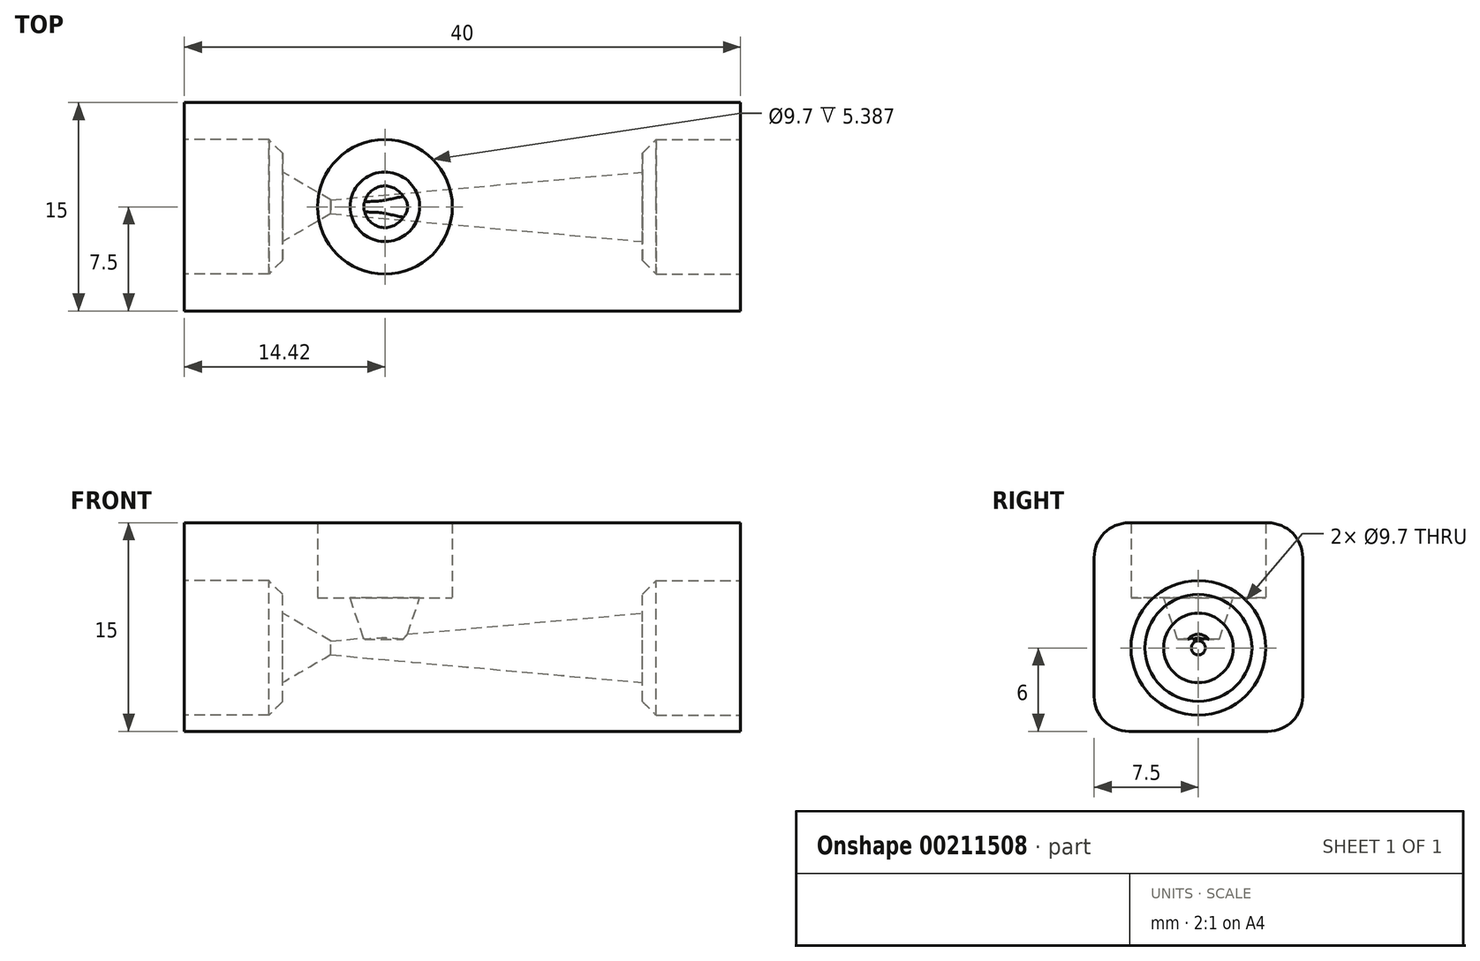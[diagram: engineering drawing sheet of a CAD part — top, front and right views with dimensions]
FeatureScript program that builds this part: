
annotation { "Feature Type Name" : "Feature", "Feature Type Description" : "" }
export const myFeature = defineFeature(function(context is Context, id is Id, definition is map)
    precondition{}
    {
        {
            var Q0;
            Q0=qCreatedBy(makeId("Right.planeOp"),FACE);
            var sketch = newSketch(context, id + "F0", { "sketchPlane" : qUnion([Q0])});
            skLineSegment(sketch, "E0.bottom", {"start": v(5, 7.5) * mm, "end": v(-5, 7.5) * mm});
            skLineSegment(sketch, "E0.top", {"start": v(5, -7.5) * mm, "end": v(-5, -7.5) * mm});
            skLineSegment(sketch, "E0.left", {"start": v(7.5, 5) * mm, "end": v(7.5, -5) * mm});
            skLineSegment(sketch, "E0.right", {"start": v(-7.5, 5) * mm, "end": v(-7.5, -5) * mm});
            skPoint(sketch, "E0.middle", {"position": v(0, 0) * mm});
            skPoint(sketch, "E1.visualSharp", {"position": v(-7.5, 7.5) * mm});
            skArc(sketch, "E1.filletArc", {"start": v(-5, 7.5) * mm, "mid": v(-6.77, 6.77) * mm, "end": v(-7.5, 5) * mm});
            skPoint(sketch, "E2.visualSharp", {"position": v(7.5, 7.5) * mm});
            skArc(sketch, "E2.filletArc", {"start": v(7.5, 5) * mm, "mid": v(6.77, 6.77) * mm, "end": v(5, 7.5) * mm});
            skPoint(sketch, "E3.visualSharp", {"position": v(7.5, -7.5) * mm});
            skArc(sketch, "E3.filletArc", {"start": v(5, -7.5) * mm, "mid": v(6.77, -6.77) * mm, "end": v(7.5, -5) * mm});
            skPoint(sketch, "E4.visualSharp", {"position": v(-7.5, -7.5) * mm});
            skArc(sketch, "E4.filletArc", {"start": v(-7.5, -5) * mm, "mid": v(-6.77, -6.77) * mm, "end": v(-5, -7.5) * mm});
            skSolve(sketch);
        }
        {
            var Q0;
            Q0=makeQuery(id+"F0.imprint","IMPRINT",FACE,{"disambiguationData":[TD([[makeQuery(id+"F0.imprint","IMPRINT",EDGE,{"derivedFrom":sQuery(id+"F0.wireOp",EDGE,"E0.left")}),-1.0]])]});
            extrude(context, id + "F1", {"entities" : qUnion([Q0]), "depth" : 40 * mm});
        }
        {
            var Q0;
            Q0=makeQuery(id+"F1.opExtrude","CAP_FACE",FACE,{"disambiguationData":[OSD([sQuery(id+"F0.wireOp",EDGE,"E0.left"),sQuery(id+"F0.wireOp",EDGE,"E0.right"),sQuery(id+"F0.wireOp",EDGE,"E1.filletArc"),sQuery(id+"F0.wireOp",EDGE,"E2.filletArc"),sQuery(id+"F0.wireOp",EDGE,"E3.filletArc"),sQuery(id+"F0.wireOp",EDGE,"E4.filletArc")])],"isStart":false});
            var sketch = newSketch(context, id + "F2", { "sketchPlane" : qUnion([Q0])});
            skCircle(sketch, "E5", {"center": v(0, -1.5) * mm, "radius": 4.85 * mm});
            skSolve(sketch);
        }
        {
            var Q0;
            Q0=makeQuery(id+"F2.imprint","IMPRINT",FACE,{"disambiguationData":[TD([[makeQuery(id+"F2.imprint","IMPRINT",EDGE,{"derivedFrom":sQuery(id+"F2.wireOp",EDGE,"pYlIlDuR-fTkt-dUTK-9zJj-bOiV4e9yzW8T")}),1.0]])]});
            var Q1;
            Q1=makeQuery(id+"F2.imprint","IMPRINT",FACE,{"disambiguationData":[TD([[makeQuery(id+"F2.imprint","IMPRINT",EDGE,{"derivedFrom":sQuery(id+"F2.wireOp",EDGE,"E5")}),1.0]])]});
            extrude(context, id + "F3", {"entities" : qUnion([Q0, Q1]), "operationType" : NewBodyOperationType.REMOVE, "oppositeDirection" : true, "depth" : 7.07 * mm});
        }
        {
            var Q0;
            Q0=makeQuery(id+"F0.imprint","IMPRINT",FACE,{"disambiguationData":[TD([[makeQuery(id+"F0.imprint","IMPRINT",EDGE,{"derivedFrom":sQuery(id+"F0.wireOp",EDGE,"E0.left")}),-1.0]])]});
            var sketch = newSketch(context, id + "F4", { "sketchPlane" : qUnion([Q0])});
            skCircle(sketch, "E6.0", {"center": v(0, -1.5) * mm, "radius": 4.85 * mm});
            skSolve(sketch);
        }
        {
            var Q0;
            Q0=makeQuery(id+"F4.imprint","IMPRINT",FACE,{"disambiguationData":[TD([[makeQuery(id+"F4.imprint","IMPRINT",EDGE,{"derivedFrom":sQuery(id+"F4.wireOp",EDGE,"E6.0")}),1.0]])]});
            extrude(context, id + "F5", {"entities" : qUnion([Q0]), "operationType" : NewBodyOperationType.REMOVE, "depth" : 7.07 * mm});
        }
        {
            var Q0;
            Q0=qCreatedBy(makeId("Front.planeOp"),FACE);
            var sketch = newSketch(context, id + "F6", { "sketchPlane" : qUnion([Q0])});
            skLineSegment(sketch, "E7", {"start": v(7.07, -1.5) * mm, "end": v(32.93, -1.5) * mm, "construction": true});
            skLineSegment(sketch, "E8", {"start": v(32.93, -1.5) * mm, "end": v(7.07, -1.5) * mm, "construction": true});
            skLineSegment(sketch, "E9", {"start": v(32.93, 1) * mm, "end": v(10.53, -1) * mm});
            skLineSegment(sketch, "E10", {"start": v(10.53, -1) * mm, "end": v(7.07, 1) * mm});
            skLineSegment(sketch, "E11", {"start": v(7.07, 1) * mm, "end": v(7.07, -1.5) * mm});
            skLineSegment(sketch, "E12", {"start": v(32.93, 1) * mm, "end": v(32.93, -1.5) * mm});
            skLineSegment(sketch, "E13", {"start": v(7.07, -1.5) * mm, "end": v(32.93, -1.5) * mm});
            skSolve(sketch);
        }
        {
            var Q0;
            Q0 = qSketchRegion(id + "F6", true);
            var Q1;
            Q1=sQuery(id+"F6.wireOp",EDGE,"E13");
            revolve(context, id + "F7", {"operationType" : NewBodyOperationType.REMOVE, "entities" : qUnion([Q0]), "axis" : qUnion([Q1]), "revolveType" : RevolveType.FULL, "oppositeDirection" : true});
        }
        {
            var Q0;
            Q0=qCreatedBy(makeId("Front.planeOp"),FACE);
            var sketch = newSketch(context, id + "F8", { "sketchPlane" : qUnion([Q0])});
            skLineSegment(sketch, "E14", {"start": v(19.27, 9.18) * mm, "end": v(19.27, 2.11) * mm});
            skLineSegment(sketch, "E15", {"start": v(19.27, 2.11) * mm, "end": v(9.57, 2.11) * mm});
            skLineSegment(sketch, "E16", {"start": v(9.57, 2.11) * mm, "end": v(9.57, 9.18) * mm});
            skLineSegment(sketch, "E17", {"start": v(11.92, 2.11) * mm, "end": v(12.92, -0.89) * mm});
            skLineSegment(sketch, "E18", {"start": v(16.92, 2.11) * mm, "end": v(16.14, -0.5) * mm});
            skLineSegment(sketch, "E19", {"start": v(14.42, 9.18) * mm, "end": v(14.42, -4.65) * mm, "construction": true});
            skPoint(sketch, "E19.startSnap0", {"position": v(14.42, 2.11) * mm});
            skLineSegment(sketch, "E20", {"start": v(12.92, -0.89) * mm, "end": v(14.42, -0.75) * mm});
            skLineSegment(sketch, "E21", {"start": v(14.42, -0.75) * mm, "end": v(14.42, 9.18) * mm});
            skLineSegment(sketch, "E22", {"start": v(9.57, 9.18) * mm, "end": v(14.42, 9.18) * mm});
            skSolve(sketch);
        }
        {
            var Q0;
            Q0 = qSketchRegion(id + "F8", true);
            var Q1;
            Q1=sQuery(id+"F8.wireOp",EDGE,"E19");
            revolve(context, id + "F9", {"operationType" : NewBodyOperationType.REMOVE, "entities" : qUnion([Q0]), "axis" : qUnion([Q1]), "revolveType" : RevolveType.FULL, "oppositeDirection" : true});
        }
        {
            var Q0;
            Q0=makeQuery(id+"F3.boolean.opBoolean","COPY",EDGE,{"derivedFrom":makeQuery(id+"F3.opExtrude","CAP_EDGE",EDGE,{"disambiguationData":[OSD([sQuery(id+"F2.wireOp",EDGE,"E5")])],"isStart":false})});
            var Q1;
            Q1=makeQuery(id+"F5.boolean.opBoolean","COPY",EDGE,{"derivedFrom":makeQuery(id+"F5.opExtrude","CAP_EDGE",EDGE,{"disambiguationData":[OSD([sQuery(id+"F4.wireOp",EDGE,"E6.0")])],"isStart":false})});
            chamfer(context, id + "F10", {"entities" : qUnion([Q0, Q1]), "width" : 1 * mm, "tangentPropagation" : true});
        }
    });
